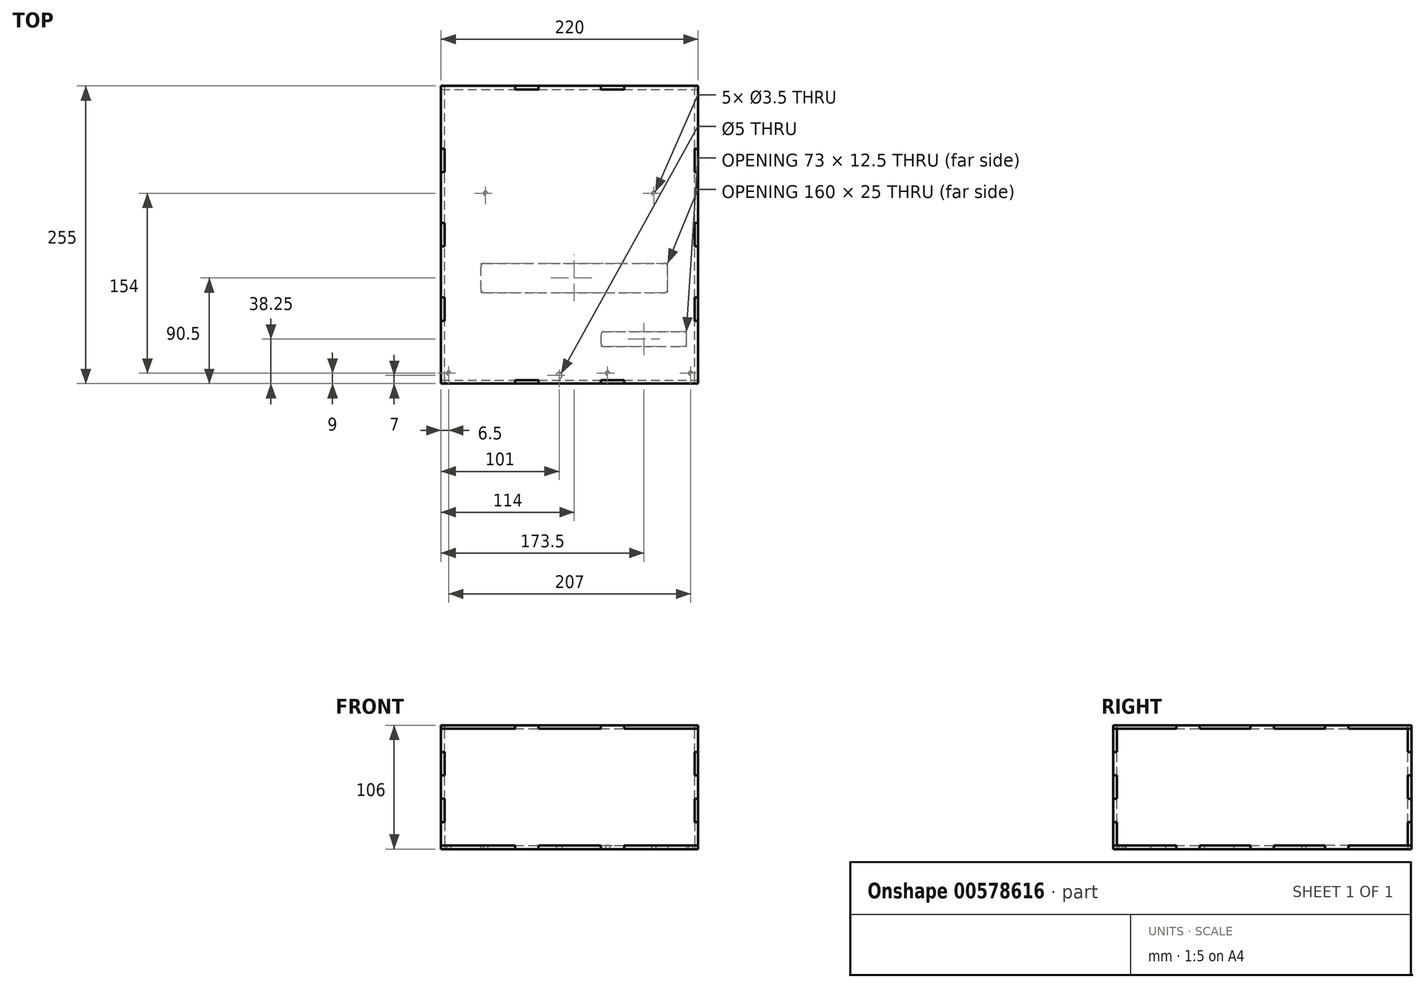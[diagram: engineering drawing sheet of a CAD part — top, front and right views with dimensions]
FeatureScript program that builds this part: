
annotation { "Feature Type Name" : "Feature", "Feature Type Description" : "" }
export const myFeature = defineFeature(function(context is Context, id is Id, definition is map)
    precondition{}
    {
        {
            assignVariable(context, id + "F0", {"name" : "Thickness", "anyValue" : 3});
        }
        {
            var Q0;
            Q0=qCreatedBy(makeId("Top.planeOp"),FACE);
            var sketch = newSketch(context, id + "F1", { "sketchPlane" : qUnion([Q0])});
            skLineSegment(sketch, "E0.bottom", {"start": v(110, -127.5) * mm, "end": v(46.67, -127.5) * mm});
            skLineSegment(sketch, "E0.top", {"start": v(110, 127.5) * mm, "end": v(46.67, 127.5) * mm});
            skLineSegment(sketch, "E0.left", {"start": v(110, -127.5) * mm, "end": v(110, -79.5) * mm});
            skLineSegment(sketch, "E0.right", {"start": v(-110, -127.5) * mm, "end": v(-110, -73.75) * mm});
            skPoint(sketch, "E0.middle", {"position": v(0, 0) * mm});
            skPoint(sketch, "E1", {"position": v(-103.5, -118.5) * mm});
            skPoint(sketch, "E2", {"position": v(103.5, -118.5) * mm});
            skPoint(sketch, "E3", {"position": v(-72, 35.5) * mm});
            skPoint(sketch, "E4", {"position": v(72, 35.5) * mm});
            skLineSegment(sketch, "E5.trimOffspring", {"start": v(110, 37.5) * mm, "end": v(110, 53.75) * mm});
            skPoint(sketch, "E6", {"position": v(32.5, -118.5) * mm});
            skLineSegment(sketch, "E7", {"start": v(110, 37.5) * mm, "end": v(110, 10) * mm});
            skLineSegment(sketch, "E8.bottom", {"start": v(-110, -73.75) * mm, "end": v(-107, -73.75) * mm});
            skLineSegment(sketch, "E8.top", {"start": v(-110, -53.75) * mm, "end": v(-107, -53.75) * mm});
            skLineSegment(sketch, "E8.right", {"start": v(-107, -73.75) * mm, "end": v(-107, -53.75) * mm});
            skLineSegment(sketch, "E9.bottom", {"start": v(-110, -10) * mm, "end": v(-107, -10) * mm});
            skLineSegment(sketch, "E9.top", {"start": v(-110, 10) * mm, "end": v(-107, 10) * mm});
            skLineSegment(sketch, "E9.right", {"start": v(-107, -10) * mm, "end": v(-107, 10) * mm});
            skLineSegment(sketch, "E10.bottom", {"start": v(-110, 73.75) * mm, "end": v(-107, 73.75) * mm});
            skLineSegment(sketch, "E10.top", {"start": v(-110, 53.75) * mm, "end": v(-107, 53.75) * mm});
            skLineSegment(sketch, "E10.right", {"start": v(-107, 73.75) * mm, "end": v(-107, 53.75) * mm});
            skLineSegment(sketch, "E11.MirrorCS", {"start": v(107, 73.75) * mm, "end": v(107, 53.75) * mm});
            skLineSegment(sketch, "E12.MirrorCS", {"start": v(110, 73.75) * mm, "end": v(107, 73.75) * mm});
            skLineSegment(sketch, "E13.MirrorCS", {"start": v(110, 53.75) * mm, "end": v(107, 53.75) * mm});
            skLineSegment(sketch, "E14.MirrorCS", {"start": v(110, 10) * mm, "end": v(107, 10) * mm});
            skLineSegment(sketch, "E15.MirrorCS", {"start": v(107, -10) * mm, "end": v(107, 10) * mm});
            skLineSegment(sketch, "E16.MirrorCS", {"start": v(110, -10) * mm, "end": v(107, -10) * mm});
            skLineSegment(sketch, "E17.MirrorCS", {"start": v(110, -53.75) * mm, "end": v(107, -53.75) * mm});
            skLineSegment(sketch, "E18.MirrorCS", {"start": v(107, -73.75) * mm, "end": v(107, -53.75) * mm});
            skLineSegment(sketch, "E19.MirrorCS", {"start": v(110, -73.75) * mm, "end": v(107, -73.75) * mm});
            skLineSegment(sketch, "E20.trimOffspring", {"start": v(110, -73.75) * mm, "end": v(110, -79.5) * mm});
            skLineSegment(sketch, "E21.trimOffspring", {"start": v(110, -10) * mm, "end": v(110, -53.75) * mm});
            skLineSegment(sketch, "E22.trimOffspring", {"start": v(110, 73.75) * mm, "end": v(110, 127.5) * mm});
            skLineSegment(sketch, "E23.trimOffspring", {"start": v(-110, 73.75) * mm, "end": v(-110, 127.5) * mm});
            skLineSegment(sketch, "E24.trimOffspring", {"start": v(-110, 10) * mm, "end": v(-110, 53.75) * mm});
            skLineSegment(sketch, "E25.trimOffspring", {"start": v(-110, -53.75) * mm, "end": v(-110, -10) * mm});
            skLineSegment(sketch, "E26.top", {"start": v(-46.67, -124.5) * mm, "end": v(-26.67, -124.5) * mm});
            skLineSegment(sketch, "E26.left", {"start": v(-46.67, -127.5) * mm, "end": v(-46.67, -124.5) * mm});
            skLineSegment(sketch, "E26.right", {"start": v(-26.67, -127.5) * mm, "end": v(-26.67, -124.5) * mm});
            skLineSegment(sketch, "E27.top", {"start": v(26.67, -124.5) * mm, "end": v(46.67, -124.5) * mm});
            skLineSegment(sketch, "E27.left", {"start": v(26.67, -127.5) * mm, "end": v(26.67, -124.5) * mm});
            skLineSegment(sketch, "E27.right", {"start": v(46.67, -127.5) * mm, "end": v(46.67, -124.5) * mm});
            skLineSegment(sketch, "E28.trimOffspring", {"start": v(-46.67, -127.5) * mm, "end": v(-110, -127.5) * mm});
            skLineSegment(sketch, "E29.trimOffspring", {"start": v(26.67, -127.5) * mm, "end": v(-26.67, -127.5) * mm});
            skLineSegment(sketch, "E30.MirrorCS", {"start": v(-46.67, 124.5) * mm, "end": v(-26.67, 124.5) * mm});
            skLineSegment(sketch, "E31.MirrorCS", {"start": v(-46.67, 127.5) * mm, "end": v(-46.67, 124.5) * mm});
            skLineSegment(sketch, "E32.MirrorCS", {"start": v(-26.67, 127.5) * mm, "end": v(-26.67, 124.5) * mm});
            skLineSegment(sketch, "E33.MirrorCS", {"start": v(26.67, 127.5) * mm, "end": v(26.67, 124.5) * mm});
            skLineSegment(sketch, "E34.MirrorCS", {"start": v(26.67, 124.5) * mm, "end": v(46.67, 124.5) * mm});
            skLineSegment(sketch, "E35.MirrorCS", {"start": v(46.67, 127.5) * mm, "end": v(46.67, 124.5) * mm});
            skLineSegment(sketch, "E36.trimOffspring", {"start": v(-46.67, 127.5) * mm, "end": v(-110, 127.5) * mm});
            skLineSegment(sketch, "E37.trimOffspring", {"start": v(26.67, 127.5) * mm, "end": v(-26.67, 127.5) * mm});
            skCircle(sketch, "E38", {"center": v(103.5, -118.5) * mm, "radius": 1.75 * mm});
            skCircle(sketch, "E39", {"center": v(32.5, -118.5) * mm, "radius": 1.75 * mm});
            skCircle(sketch, "E40", {"center": v(-103.5, -118.5) * mm, "radius": 1.75 * mm});
            skCircle(sketch, "E41", {"center": v(-72, 35.5) * mm, "radius": 1.75 * mm});
            skCircle(sketch, "E42", {"center": v(72, 35.5) * mm, "radius": 1.75 * mm});
            skLineSegment(sketch, "E43.bottom", {"start": v(-73, -49.5) * mm, "end": v(81, -49.5) * mm});
            skLineSegment(sketch, "E43.top", {"start": v(-73, -24.5) * mm, "end": v(81, -24.5) * mm});
            skLineSegment(sketch, "E43.left", {"start": v(-76, -46.5) * mm, "end": v(-76, -27.5) * mm});
            skLineSegment(sketch, "E43.right", {"start": v(84, -46.5) * mm, "end": v(84, -27.5) * mm});
            skLineSegment(sketch, "E44.bottom", {"start": v(29, -95.5) * mm, "end": v(98, -95.5) * mm});
            skLineSegment(sketch, "E44.top", {"start": v(29, -83) * mm, "end": v(98, -83) * mm});
            skLineSegment(sketch, "E44.left", {"start": v(27, -93.5) * mm, "end": v(27, -85) * mm});
            skLineSegment(sketch, "E44.right", {"start": v(100, -93.5) * mm, "end": v(100, -85) * mm});
            skPoint(sketch, "E45.visualSharp", {"position": v(-76, -24.5) * mm});
            skArc(sketch, "E45.filletArc", {"start": v(-73, -24.5) * mm, "mid": v(-75.12, -25.38) * mm, "end": v(-76, -27.5) * mm});
            skPoint(sketch, "E46.visualSharp", {"position": v(84, -24.5) * mm});
            skArc(sketch, "E46.filletArc", {"start": v(84, -27.5) * mm, "mid": v(83.12, -25.38) * mm, "end": v(81, -24.5) * mm});
            skPoint(sketch, "E47.visualSharp", {"position": v(84, -49.5) * mm});
            skArc(sketch, "E47.filletArc", {"start": v(81, -49.5) * mm, "mid": v(83.12, -48.62) * mm, "end": v(84, -46.5) * mm});
            skPoint(sketch, "E48.visualSharp", {"position": v(-76, -49.5) * mm});
            skArc(sketch, "E48.filletArc", {"start": v(-76, -46.5) * mm, "mid": v(-75.12, -48.62) * mm, "end": v(-73, -49.5) * mm});
            skPoint(sketch, "E49.visualSharp", {"position": v(27, -83) * mm});
            skArc(sketch, "E49.filletArc", {"start": v(29, -83) * mm, "mid": v(27.59, -83.59) * mm, "end": v(27, -85) * mm});
            skPoint(sketch, "E50.visualSharp", {"position": v(100, -83) * mm});
            skArc(sketch, "E50.filletArc", {"start": v(100, -85) * mm, "mid": v(99.41, -83.59) * mm, "end": v(98, -83) * mm});
            skPoint(sketch, "E51.visualSharp", {"position": v(100, -95.5) * mm});
            skArc(sketch, "E51.filletArc", {"start": v(98, -95.5) * mm, "mid": v(99.41, -94.91) * mm, "end": v(100, -93.5) * mm});
            skPoint(sketch, "E52.visualSharp", {"position": v(27, -95.5) * mm});
            skArc(sketch, "E52.filletArc", {"start": v(27, -93.5) * mm, "mid": v(27.59, -94.91) * mm, "end": v(29, -95.5) * mm});
            skCircle(sketch, "E53", {"center": v(-9, -120.5) * mm, "radius": 2.5 * mm});
            skSolve(sketch);
        }
        {
            var Q0;
            Q0 = qSketchRegion(id + "F1", true);
            extrude(context, id + "F2", {"entities" : qUnion([Q0]), "depth" : (getVariable(context, 'Thickness')) * mm, "offsetDistance" : 25 * mm});
        }
        {
            var Q0;
            Q0=makeQuery(id+"F2.opExtrude","SWEPT_FACE",FACE,{"disambiguationData":[OSD([sQuery(id+"F1.wireOp",EDGE,"E28.trimOffspring")])]});
            var sketch = newSketch(context, id + "F3", { "sketchPlane" : qUnion([Q0])});
            skLineSegment(sketch, "E54.bottom", {"start": v(-110, 3) * mm, "end": v(-46.67, 3) * mm});
            skLineSegment(sketch, "E54.top", {"start": v(-110, 103) * mm, "end": v(-46.67, 103) * mm});
            skLineSegment(sketch, "E54.left", {"start": v(-110, 3) * mm, "end": v(-110, 23) * mm});
            skLineSegment(sketch, "E54.right", {"start": v(110, 3) * mm, "end": v(110, 23) * mm});
            skLineSegment(sketch, "E55.top", {"start": v(-46.67, 0) * mm, "end": v(-26.67, 0) * mm});
            skLineSegment(sketch, "E55.left", {"start": v(-46.67, 3) * mm, "end": v(-46.67, 0) * mm});
            skLineSegment(sketch, "E55.right", {"start": v(-26.67, 3) * mm, "end": v(-26.67, 0) * mm});
            skLineSegment(sketch, "E56.trimOffspring", {"start": v(-26.67, 3) * mm, "end": v(26.67, 3) * mm});
            skLineSegment(sketch, "E57.top", {"start": v(26.67, 0) * mm, "end": v(46.67, 0) * mm});
            skLineSegment(sketch, "E57.left", {"start": v(26.67, 3) * mm, "end": v(26.67, 0) * mm});
            skLineSegment(sketch, "E57.right", {"start": v(46.67, 3) * mm, "end": v(46.67, 0) * mm});
            skLineSegment(sketch, "E58.trimOffspring", {"start": v(46.67, 3) * mm, "end": v(110, 3) * mm});
            skLineSegment(sketch, "E59.bottom", {"start": v(110, 23) * mm, "end": v(107, 23) * mm});
            skLineSegment(sketch, "E59.top", {"start": v(110, 43) * mm, "end": v(107, 43) * mm});
            skLineSegment(sketch, "E59.right", {"start": v(107, 23) * mm, "end": v(107, 43) * mm});
            skLineSegment(sketch, "E60.bottom", {"start": v(110, 63) * mm, "end": v(107, 63) * mm});
            skLineSegment(sketch, "E60.top", {"start": v(110, 83) * mm, "end": v(107, 83) * mm});
            skLineSegment(sketch, "E60.right", {"start": v(107, 63) * mm, "end": v(107, 83) * mm});
            skLineSegment(sketch, "E61.MirrorCS", {"start": v(-110, 83) * mm, "end": v(-107, 83) * mm});
            skLineSegment(sketch, "E62.MirrorCS", {"start": v(-107, 63) * mm, "end": v(-107, 83) * mm});
            skLineSegment(sketch, "E63.MirrorCS", {"start": v(-110, 63) * mm, "end": v(-107, 63) * mm});
            skLineSegment(sketch, "E64.MirrorCS", {"start": v(-107, 23) * mm, "end": v(-107, 43) * mm});
            skLineSegment(sketch, "E65.MirrorCS", {"start": v(-110, 23) * mm, "end": v(-107, 23) * mm});
            skLineSegment(sketch, "E66.MirrorCS", {"start": v(-110, 43) * mm, "end": v(-107, 43) * mm});
            skLineSegment(sketch, "E67.trimOffspring", {"start": v(-110, 83) * mm, "end": v(-110, 103) * mm});
            skLineSegment(sketch, "E68.trimOffspring", {"start": v(-110, 43) * mm, "end": v(-110, 63) * mm});
            skLineSegment(sketch, "E69.trimOffspring", {"start": v(110, 43) * mm, "end": v(110, 63) * mm});
            skLineSegment(sketch, "E70.trimOffspring", {"start": v(110, 83) * mm, "end": v(110, 103) * mm});
            skLineSegment(sketch, "E71.MirrorCS", {"start": v(-46.67, -3) * mm, "end": v(-46.67, 0) * mm});
            skLineSegment(sketch, "E72.MirrorCS", {"start": v(-26.67, -3) * mm, "end": v(-26.67, 0) * mm});
            skLineSegment(sketch, "E73.MirrorCS", {"start": v(26.67, -3) * mm, "end": v(26.67, 0) * mm});
            skLineSegment(sketch, "E74.MirrorCS", {"start": v(46.67, -3) * mm, "end": v(46.67, 0) * mm});
            skLineSegment(sketch, "E75.MirrorCS", {"start": v(-46.67, 106) * mm, "end": v(-26.67, 106) * mm});
            skLineSegment(sketch, "E76.MirrorCS", {"start": v(-46.67, 103) * mm, "end": v(-46.67, 106) * mm});
            skLineSegment(sketch, "E77.MirrorCS", {"start": v(-26.67, 103) * mm, "end": v(-26.67, 106) * mm});
            skLineSegment(sketch, "E78.MirrorCS", {"start": v(26.67, 103) * mm, "end": v(26.67, 106) * mm});
            skLineSegment(sketch, "E79.MirrorCS", {"start": v(46.67, 103) * mm, "end": v(46.67, 106) * mm});
            skLineSegment(sketch, "E80.MirrorCS", {"start": v(26.67, 106) * mm, "end": v(46.67, 106) * mm});
            skLineSegment(sketch, "E81.trimOffspring", {"start": v(-26.67, 103) * mm, "end": v(26.67, 103) * mm});
            skPoint(sketch, "E82.end.orphan", {"position": v(110, 53) * mm});
            skPoint(sketch, "E82.start.orphan", {"position": v(-110, 53) * mm});
            skLineSegment(sketch, "E83.trimOffspring", {"start": v(46.67, 103) * mm, "end": v(110, 103) * mm});
            skSolve(sketch);
        }
        {
            var Q0;
            Q0=makeQuery(id+"F3.imprint","IMPRINT",FACE,{"disambiguationData":[TD([[makeQuery(id+"F3.imprint","IMPRINT",EDGE,{"derivedFrom":sQuery(id+"F3.wireOp",EDGE,"E54.bottom")}),-1.0]])]});
            extrude(context, id + "F4", {"entities" : qUnion([Q0]), "oppositeDirection" : true, "depth" : (getVariable(context, 'Thickness')) * mm, "offsetDistance" : 25 * mm});
        }
        {
            var Q0;
            Q0=makeQuery(id+"F2.opExtrude","SWEPT_FACE",FACE,{"disambiguationData":[OSD([sQuery(id+"F1.wireOp",EDGE,"E0.left"),sQuery(id+"F1.wireOp",EDGE,"E20.trimOffspring")])]});
            var sketch = newSketch(context, id + "F5", { "sketchPlane" : qUnion([Q0])});
            skLineSegment(sketch, "E84.bottom", {"start": v(-124.5, 3) * mm, "end": v(-73.75, 3) * mm});
            skLineSegment(sketch, "E84.top", {"start": v(-124.5, 103) * mm, "end": v(-73.75, 103) * mm});
            skLineSegment(sketch, "E85.top", {"start": v(-73.75, 0) * mm, "end": v(-53.75, 0) * mm});
            skLineSegment(sketch, "E85.left", {"start": v(-73.75, 3) * mm, "end": v(-73.75, 0) * mm});
            skLineSegment(sketch, "E85.right", {"start": v(-53.75, 3) * mm, "end": v(-53.75, 0) * mm});
            skLineSegment(sketch, "E86.top", {"start": v(-10, 0) * mm, "end": v(10, 0) * mm});
            skLineSegment(sketch, "E86.left", {"start": v(-10, 3) * mm, "end": v(-10, 0) * mm});
            skLineSegment(sketch, "E86.right", {"start": v(10, 3) * mm, "end": v(10, 0) * mm});
            skLineSegment(sketch, "E87.top", {"start": v(53.75, 0) * mm, "end": v(73.75, 0) * mm});
            skLineSegment(sketch, "E87.left", {"start": v(53.75, 3) * mm, "end": v(53.75, 0) * mm});
            skLineSegment(sketch, "E87.right", {"start": v(73.75, 3) * mm, "end": v(73.75, 0) * mm});
            skLineSegment(sketch, "E88.trimOffspring", {"start": v(73.75, 3) * mm, "end": v(124.5, 3) * mm});
            skLineSegment(sketch, "E89.trimOffspring", {"start": v(10, 3) * mm, "end": v(53.75, 3) * mm});
            skLineSegment(sketch, "E90.trimOffspring", {"start": v(-53.75, 3) * mm, "end": v(-10, 3) * mm});
            skLineSegment(sketch, "E91.MirrorCS", {"start": v(127.5, 83) * mm, "end": v(124.5, 83) * mm});
            skLineSegment(sketch, "E92.MirrorCS", {"start": v(127.5, 63) * mm, "end": v(124.5, 63) * mm});
            skLineSegment(sketch, "E93.MirrorCS", {"start": v(127.5, 43) * mm, "end": v(124.5, 43) * mm});
            skLineSegment(sketch, "E94.MirrorCS", {"start": v(127.5, 23) * mm, "end": v(124.5, 23) * mm});
            skLineSegment(sketch, "E95", {"start": v(-127.5, 83) * mm, "end": v(-127.5, 63) * mm});
            skLineSegment(sketch, "E96", {"start": v(-127.5, 43) * mm, "end": v(-127.5, 23) * mm});
            skLineSegment(sketch, "E97.bottom", {"start": v(-127.5, 23) * mm, "end": v(-124.5, 23) * mm});
            skLineSegment(sketch, "E97.right", {"start": v(-124.5, 23) * mm, "end": v(-124.5, 3) * mm});
            skLineSegment(sketch, "E98.bottom", {"start": v(-127.5, 43) * mm, "end": v(-124.5, 43) * mm});
            skLineSegment(sketch, "E98.top", {"start": v(-127.5, 63) * mm, "end": v(-124.5, 63) * mm});
            skLineSegment(sketch, "E98.right", {"start": v(-124.5, 43) * mm, "end": v(-124.5, 63) * mm});
            skLineSegment(sketch, "E99.bottom", {"start": v(-127.5, 83) * mm, "end": v(-124.5, 83) * mm});
            skLineSegment(sketch, "E99.right", {"start": v(-124.5, 83) * mm, "end": v(-124.5, 103) * mm});
            skLineSegment(sketch, "E100.MirrorCS", {"start": v(124.5, 23) * mm, "end": v(124.5, 3) * mm});
            skLineSegment(sketch, "E101.MirrorCS", {"start": v(124.5, 43) * mm, "end": v(124.5, 63) * mm});
            skLineSegment(sketch, "E102.MirrorCS", {"start": v(124.5, 83) * mm, "end": v(124.5, 103) * mm});
            skLineSegment(sketch, "E103", {"start": v(127.5, 23) * mm, "end": v(127.5, 43) * mm});
            skLineSegment(sketch, "E104", {"start": v(127.5, 83) * mm, "end": v(127.5, 63) * mm});
            skLineSegment(sketch, "E105.MirrorCS", {"start": v(-73.75, 106) * mm, "end": v(-53.75, 106) * mm});
            skLineSegment(sketch, "E106.MirrorCS", {"start": v(-73.75, 103) * mm, "end": v(-73.75, 106) * mm});
            skLineSegment(sketch, "E107.MirrorCS", {"start": v(-53.75, 103) * mm, "end": v(-53.75, 106) * mm});
            skLineSegment(sketch, "E108.MirrorCS", {"start": v(-10, 103) * mm, "end": v(-10, 106) * mm});
            skLineSegment(sketch, "E109.MirrorCS", {"start": v(-10, 106) * mm, "end": v(10, 106) * mm});
            skLineSegment(sketch, "E110.MirrorCS", {"start": v(10, 103) * mm, "end": v(10, 106) * mm});
            skLineSegment(sketch, "E111.MirrorCS", {"start": v(53.75, 103) * mm, "end": v(53.75, 106) * mm});
            skLineSegment(sketch, "E112.MirrorCS", {"start": v(53.75, 106) * mm, "end": v(73.75, 106) * mm});
            skLineSegment(sketch, "E113.MirrorCS", {"start": v(73.75, 103) * mm, "end": v(73.75, 106) * mm});
            skPoint(sketch, "E114.end.orphan", {"position": v(124.5, 53) * mm});
            skPoint(sketch, "E114.start.orphan", {"position": v(-124.5, 53) * mm});
            skLineSegment(sketch, "E115.trimOffspring", {"start": v(-53.75, 103) * mm, "end": v(-10, 103) * mm});
            skLineSegment(sketch, "E116.trimOffspring", {"start": v(10, 103) * mm, "end": v(53.75, 103) * mm});
            skLineSegment(sketch, "E117.trimOffspring", {"start": v(73.75, 103) * mm, "end": v(124.5, 103) * mm});
            skSolve(sketch);
        }
        {
            var Q0;
            Q0=makeQuery(id+"F5.imprint","IMPRINT",FACE,{"disambiguationData":[TD([[makeQuery(id+"F5.imprint","IMPRINT",EDGE,{"derivedFrom":sQuery(id+"F5.wireOp",EDGE,"E84.bottom")}),1.0]])]});
            extrude(context, id + "F6", {"entities" : qUnion([Q0]), "oppositeDirection" : true, "depth" : (getVariable(context, 'Thickness')) * mm, "offsetDistance" : 25 * mm});
        }
        {
            var Q0;
            Q0=makeQuery(id+"F4.opExtrude","SWEPT_BODY",BODY,{"disambiguationData":[OSD([sQuery(id+"F3.wireOp",EDGE,"E54.bottom"),sQuery(id+"F3.wireOp",EDGE,"E54.top"),sQuery(id+"F3.wireOp",EDGE,"E54.left"),sQuery(id+"F3.wireOp",EDGE,"E54.right"),sQuery(id+"F3.wireOp",EDGE,"E55.top"),sQuery(id+"F3.wireOp",EDGE,"E55.left"),sQuery(id+"F3.wireOp",EDGE,"E55.right"),sQuery(id+"F3.wireOp",EDGE,"E56.trimOffspring"),sQuery(id+"F3.wireOp",EDGE,"E57.top"),sQuery(id+"F3.wireOp",EDGE,"E57.left"),sQuery(id+"F3.wireOp",EDGE,"E57.right"),sQuery(id+"F3.wireOp",EDGE,"E58.trimOffspring"),sQuery(id+"F3.wireOp",EDGE,"E59.bottom"),sQuery(id+"F3.wireOp",EDGE,"E59.top"),sQuery(id+"F3.wireOp",EDGE,"E59.right"),sQuery(id+"F3.wireOp",EDGE,"E60.bottom"),sQuery(id+"F3.wireOp",EDGE,"E60.top"),sQuery(id+"F3.wireOp",EDGE,"E60.right"),sQuery(id+"F3.wireOp",EDGE,"E61.MirrorCS"),sQuery(id+"F3.wireOp",EDGE,"E62.MirrorCS"),sQuery(id+"F3.wireOp",EDGE,"E63.MirrorCS"),sQuery(id+"F3.wireOp",EDGE,"E64.MirrorCS"),sQuery(id+"F3.wireOp",EDGE,"E65.MirrorCS"),sQuery(id+"F3.wireOp",EDGE,"E66.MirrorCS"),sQuery(id+"F3.wireOp",EDGE,"E67.trimOffspring"),sQuery(id+"F3.wireOp",EDGE,"E68.trimOffspring"),sQuery(id+"F3.wireOp",EDGE,"E69.trimOffspring"),sQuery(id+"F3.wireOp",EDGE,"E70.trimOffspring")])]});
            var Q1;
            Q1=qCreatedBy(makeId("Front.planeOp"),FACE);
            mirror(context, id + "F7", {"entities" : qUnion([Q0]), "mirrorPlane" : qUnion([Q1])});
        }
        {
            var Q0;
            Q0=makeQuery(id+"F6.opExtrude","SWEPT_BODY",BODY,{"disambiguationData":[OSD([sQuery(id+"F5.wireOp",EDGE,"E84.bottom"),sQuery(id+"F5.wireOp",EDGE,"E84.top"),sQuery(id+"F5.wireOp",EDGE,"E85.top"),sQuery(id+"F5.wireOp",EDGE,"E85.left"),sQuery(id+"F5.wireOp",EDGE,"E85.right"),sQuery(id+"F5.wireOp",EDGE,"E86.top"),sQuery(id+"F5.wireOp",EDGE,"E86.left"),sQuery(id+"F5.wireOp",EDGE,"E86.right"),sQuery(id+"F5.wireOp",EDGE,"E87.top"),sQuery(id+"F5.wireOp",EDGE,"E87.left"),sQuery(id+"F5.wireOp",EDGE,"E87.right"),sQuery(id+"F5.wireOp",EDGE,"E88.trimOffspring"),sQuery(id+"F5.wireOp",EDGE,"E89.trimOffspring"),sQuery(id+"F5.wireOp",EDGE,"E90.trimOffspring"),sQuery(id+"F5.wireOp",EDGE,"E95"),sQuery(id+"F5.wireOp",EDGE,"E96"),sQuery(id+"F5.wireOp",EDGE,"E97.bottom"),sQuery(id+"F5.wireOp",EDGE,"E97.right"),sQuery(id+"F5.wireOp",EDGE,"E98.bottom"),sQuery(id+"F5.wireOp",EDGE,"E98.top"),sQuery(id+"F5.wireOp",EDGE,"E98.right"),sQuery(id+"F5.wireOp",EDGE,"E99.bottom"),sQuery(id+"F5.wireOp",EDGE,"E99.right"),sQuery(id+"F5.wireOp",EDGE,"E100.MirrorCS"),sQuery(id+"F5.wireOp",EDGE,"E94.MirrorCS"),sQuery(id+"F5.wireOp",EDGE,"E101.MirrorCS"),sQuery(id+"F5.wireOp",EDGE,"E93.MirrorCS"),sQuery(id+"F5.wireOp",EDGE,"E92.MirrorCS"),sQuery(id+"F5.wireOp",EDGE,"E91.MirrorCS"),sQuery(id+"F5.wireOp",EDGE,"E102.MirrorCS"),sQuery(id+"F5.wireOp",EDGE,"E103"),sQuery(id+"F5.wireOp",EDGE,"E104")])]});
            var Q1;
            Q1=qCreatedBy(makeId("Right.planeOp"),FACE);
            mirror(context, id + "F8", {"entities" : qUnion([Q0]), "mirrorPlane" : qUnion([Q1])});
        }
        {
            var Q0;
            Q0=makeQuery(id+"F4.opExtrude","SWEPT_FACE",FACE,{"disambiguationData":[OSD([sQuery(id+"F3.wireOp",EDGE,"E75.MirrorCS")])]});
            var sketch = newSketch(context, id + "F9", { "sketchPlane" : qUnion([Q0])});
            skLineSegment(sketch, "E118.bottom", {"start": v(-110, -127.5) * mm, "end": v(-46.67, -127.5) * mm});
            skLineSegment(sketch, "E118.top", {"start": v(-110, 127.5) * mm, "end": v(-46.67, 127.5) * mm});
            skLineSegment(sketch, "E118.left", {"start": v(-110, -127.5) * mm, "end": v(-110, -73.75) * mm});
            skLineSegment(sketch, "E118.right", {"start": v(110, -127.5) * mm, "end": v(110, -73.75) * mm});
            skLineSegment(sketch, "E119.top", {"start": v(-46.67, -124.5) * mm, "end": v(-26.67, -124.5) * mm});
            skLineSegment(sketch, "E119.left", {"start": v(-46.67, -127.5) * mm, "end": v(-46.67, -124.5) * mm});
            skLineSegment(sketch, "E119.right", {"start": v(-26.67, -127.5) * mm, "end": v(-26.67, -124.5) * mm});
            skLineSegment(sketch, "E120.top", {"start": v(26.67, -124.5) * mm, "end": v(46.67, -124.5) * mm});
            skLineSegment(sketch, "E120.left", {"start": v(26.67, -127.5) * mm, "end": v(26.67, -124.5) * mm});
            skLineSegment(sketch, "E120.right", {"start": v(46.67, -127.5) * mm, "end": v(46.67, -124.5) * mm});
            skLineSegment(sketch, "E121.trimOffspring", {"start": v(-26.67, -127.5) * mm, "end": v(26.67, -127.5) * mm});
            skLineSegment(sketch, "E122.trimOffspring", {"start": v(46.67, -127.5) * mm, "end": v(110, -127.5) * mm});
            skLineSegment(sketch, "E123.MirrorCS", {"start": v(-46.67, 124.5) * mm, "end": v(-26.67, 124.5) * mm});
            skLineSegment(sketch, "E124.MirrorCS", {"start": v(-46.67, 127.5) * mm, "end": v(-46.67, 124.5) * mm});
            skLineSegment(sketch, "E125.MirrorCS", {"start": v(-26.67, 127.5) * mm, "end": v(-26.67, 124.5) * mm});
            skLineSegment(sketch, "E126.MirrorCS", {"start": v(26.67, 127.5) * mm, "end": v(26.67, 124.5) * mm});
            skLineSegment(sketch, "E127.MirrorCS", {"start": v(26.67, 124.5) * mm, "end": v(46.67, 124.5) * mm});
            skLineSegment(sketch, "E128.MirrorCS", {"start": v(46.67, 127.5) * mm, "end": v(46.67, 124.5) * mm});
            skLineSegment(sketch, "E129.trimOffspring", {"start": v(-26.67, 127.5) * mm, "end": v(26.67, 127.5) * mm});
            skLineSegment(sketch, "E130.trimOffspring", {"start": v(46.67, 127.5) * mm, "end": v(110, 127.5) * mm});
            skLineSegment(sketch, "E131.bottom", {"start": v(-110, -73.75) * mm, "end": v(-107, -73.75) * mm});
            skLineSegment(sketch, "E131.top", {"start": v(-110, -53.75) * mm, "end": v(-107, -53.75) * mm});
            skLineSegment(sketch, "E131.right", {"start": v(-107, -73.75) * mm, "end": v(-107, -53.75) * mm});
            skLineSegment(sketch, "E132.trimOffspring", {"start": v(-110, -53.75) * mm, "end": v(-110, -10) * mm});
            skLineSegment(sketch, "E133.bottom", {"start": v(-110, -10) * mm, "end": v(-107, -10) * mm});
            skLineSegment(sketch, "E133.top", {"start": v(-110, 10) * mm, "end": v(-107, 10) * mm});
            skLineSegment(sketch, "E133.right", {"start": v(-107, -10) * mm, "end": v(-107, 10) * mm});
            skLineSegment(sketch, "E134.trimOffspring", {"start": v(-110, 10) * mm, "end": v(-110, 53.75) * mm});
            skLineSegment(sketch, "E135.bottom", {"start": v(-110, 53.75) * mm, "end": v(-107, 53.75) * mm});
            skLineSegment(sketch, "E135.top", {"start": v(-110, 73.75) * mm, "end": v(-107, 73.75) * mm});
            skLineSegment(sketch, "E135.right", {"start": v(-107, 53.75) * mm, "end": v(-107, 73.75) * mm});
            skLineSegment(sketch, "E136.trimOffspring", {"start": v(-110, 73.75) * mm, "end": v(-110, 127.5) * mm});
            skLineSegment(sketch, "E137.MirrorCS", {"start": v(110, 73.75) * mm, "end": v(107, 73.75) * mm});
            skLineSegment(sketch, "E138.MirrorCS", {"start": v(107, 53.75) * mm, "end": v(107, 73.75) * mm});
            skLineSegment(sketch, "E139.MirrorCS", {"start": v(110, 53.75) * mm, "end": v(107, 53.75) * mm});
            skLineSegment(sketch, "E140.MirrorCS", {"start": v(110, 10) * mm, "end": v(107, 10) * mm});
            skLineSegment(sketch, "E141.MirrorCS", {"start": v(107, -10) * mm, "end": v(107, 10) * mm});
            skLineSegment(sketch, "E142.MirrorCS", {"start": v(110, -10) * mm, "end": v(107, -10) * mm});
            skLineSegment(sketch, "E143.MirrorCS", {"start": v(110, -53.75) * mm, "end": v(107, -53.75) * mm});
            skLineSegment(sketch, "E144.MirrorCS", {"start": v(107, -73.75) * mm, "end": v(107, -53.75) * mm});
            skLineSegment(sketch, "E145.MirrorCS", {"start": v(110, -73.75) * mm, "end": v(107, -73.75) * mm});
            skLineSegment(sketch, "E146.trimOffspring", {"start": v(110, -53.75) * mm, "end": v(110, -10) * mm});
            skLineSegment(sketch, "E147.trimOffspring", {"start": v(110, 10) * mm, "end": v(110, 53.75) * mm});
            skLineSegment(sketch, "E148.trimOffspring", {"start": v(110, 73.75) * mm, "end": v(110, 127.5) * mm});
            skSolve(sketch);
        }
        {
            var Q0;
            Q0=makeQuery(id+"F9.imprint","IMPRINT",FACE,{"disambiguationData":[TD([[makeQuery(id+"F9.imprint","IMPRINT",EDGE,{"derivedFrom":sQuery(id+"F9.wireOp",EDGE,"E118.bottom")}),1.0]])]});
            extrude(context, id + "F10", {"entities" : qUnion([Q0]), "oppositeDirection" : true, "depth" : (getVariable(context, 'Thickness')) * mm, "offsetDistance" : 25 * mm});
        }
    });
